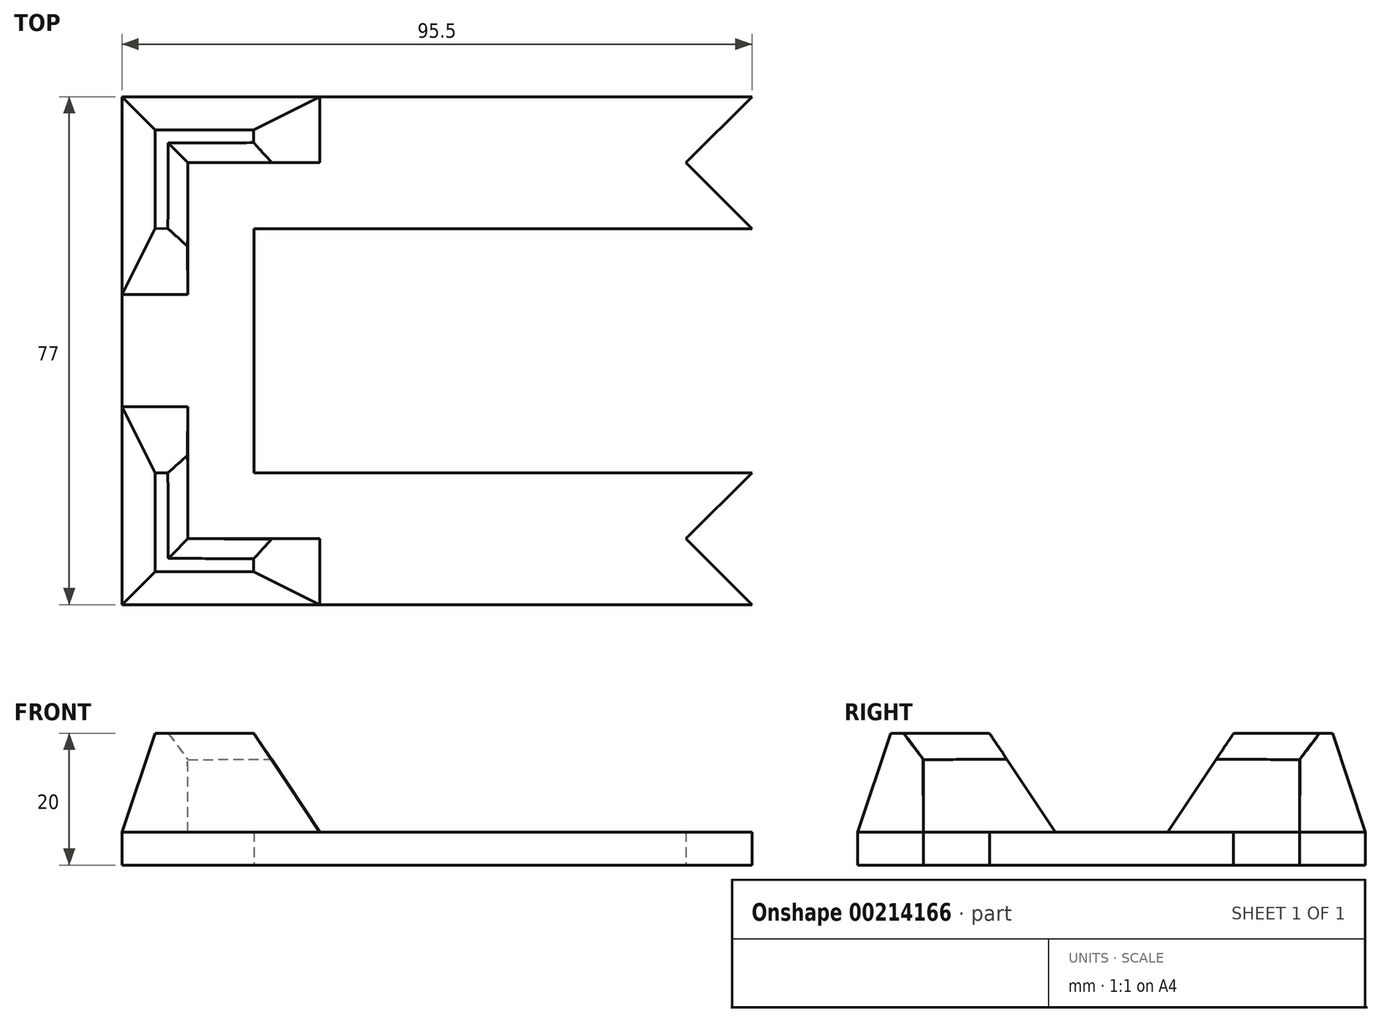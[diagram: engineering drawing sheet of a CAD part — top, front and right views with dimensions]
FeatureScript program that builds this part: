
annotation { "Feature Type Name" : "Feature", "Feature Type Description" : "" }
export const myFeature = defineFeature(function(context is Context, id is Id, definition is map)
    precondition{}
    {
        {
            var Q0;
            Q0=qCreatedBy(makeId("Top.planeOp"),FACE);
            var sketch = newSketch(context, id + "F0", { "sketchPlane" : qUnion([Q0])});
            skLineSegment(sketch, "E0.bottom", {"start": v(75.5, -28.5) * mm, "end": v(-75.5, -28.5) * mm, "construction": true});
            skLineSegment(sketch, "E0.top", {"start": v(75.5, 28.5) * mm, "end": v(-75.5, 28.5) * mm, "construction": true});
            skLineSegment(sketch, "E0.left", {"start": v(75.5, -28.5) * mm, "end": v(75.5, 28.5) * mm, "construction": true});
            skLineSegment(sketch, "E0.right", {"start": v(-75.5, -28.5) * mm, "end": v(-75.5, 28.5) * mm, "construction": true});
            skPoint(sketch, "E0.middle", {"position": v(0, 0) * mm});
            skLineSegment(sketch, "E1.bottom", {"start": v(85.5, -38.5) * mm, "end": v(-85.5, -38.5) * mm});
            skLineSegment(sketch, "E1.top", {"start": v(85.5, 38.5) * mm, "end": v(-85.5, 38.5) * mm});
            skLineSegment(sketch, "E1.left", {"start": v(85.5, -38.5) * mm, "end": v(85.5, 38.5) * mm});
            skLineSegment(sketch, "E1.right", {"start": v(-85.5, -38.5) * mm, "end": v(-85.5, 38.5) * mm});
            skSolve(sketch);
        }
        {
            var Q0;
            Q0=qCreatedBy(makeId("Top.planeOp"),FACE);
            cPlane(context, id + "F1", {"entities" : qUnion([Q0]), "cplaneType" : CPlaneType.OFFSET, "offset" : 15 * mm, "width" : 150 * mm, "height" : 150 * mm});
        }
        {
            var Q0;
            Q0=qCreatedBy(id+"F1.planeOp",FACE);
            var sketch = newSketch(context, id + "F2", { "sketchPlane" : qUnion([Q0])});
            skPoint(sketch, "E2.0", {"position": v(-85.5, -38.5) * mm});
            skPoint(sketch, "E3.0", {"position": v(-75.5, -28.5) * mm});
            skLineSegment(sketch, "E4", {"start": v(-75.58, -18.5) * mm, "end": v(-75.5, -28.5) * mm});
            skLineSegment(sketch, "E5", {"start": v(-75.5, -28.5) * mm, "end": v(-85.5, -38.5) * mm, "construction": true});
            skPoint(sketch, "E6", {"position": v(-80.5, -33.5) * mm});
            skLineSegment(sketch, "E7", {"start": v(-75.58, -18.5) * mm, "end": v(-80.5, -18.54) * mm});
            skLineSegment(sketch, "E8", {"start": v(-80.5, -18.54) * mm, "end": v(-80.5, -33.5) * mm});
            skLineSegment(sketch, "E9.MirrorCS", {"start": v(-65.54, -33.5) * mm, "end": v(-80.5, -33.5) * mm});
            skLineSegment(sketch, "E10.MirrorCS", {"start": v(-65.5, -28.58) * mm, "end": v(-65.54, -33.5) * mm});
            skLineSegment(sketch, "E11.MirrorCS", {"start": v(-65.5, -28.58) * mm, "end": v(-75.5, -28.5) * mm});
            skSolve(sketch);
        }
        {
            var Q0;
            Q0=qCreatedBy(makeId("Top.planeOp"),FACE);
            var sketch = newSketch(context, id + "F3", { "sketchPlane" : qUnion([Q0])});
            skPoint(sketch, "E12.0", {"position": v(-85.5, -38.5) * mm});
            skPoint(sketch, "E13.0", {"position": v(-75.5, -28.5) * mm});
            skLineSegment(sketch, "E14", {"start": v(-85.5, -38.5) * mm, "end": v(-85.5, -8.5) * mm});
            skLineSegment(sketch, "E15", {"start": v(-85.5, -8.5) * mm, "end": v(-75.5, -8.5) * mm});
            skLineSegment(sketch, "E16", {"start": v(-75.5, -8.5) * mm, "end": v(-75.5, -28.5) * mm});
            skLineSegment(sketch, "E17", {"start": v(-75.5, -28.5) * mm, "end": v(-85.5, -38.5) * mm, "construction": true});
            skLineSegment(sketch, "E18.MirrorCS", {"start": v(-55.5, -28.5) * mm, "end": v(-75.5, -28.5) * mm});
            skLineSegment(sketch, "E19.MirrorCS", {"start": v(-85.5, -38.5) * mm, "end": v(-55.5, -38.5) * mm});
            skLineSegment(sketch, "E20.MirrorCS", {"start": v(-55.5, -38.5) * mm, "end": v(-55.5, -28.5) * mm});
            skSolve(sketch);
        }
        {
            var Q0;
            Q0=makeQuery(id+"F0.imprint","IMPRINT",FACE,{"disambiguationData":[TD([[makeQuery(id+"F0.imprint","IMPRINT",EDGE,{"derivedFrom":sQuery(id+"F0.wireOp",EDGE,"E1.bottom")}),-1.0]])]});
            extrude(context, id + "F4", {"entities" : qUnion([Q0]), "oppositeDirection" : true, "depth" : 5 * mm});
        }
        {
            var Q1;
            Q1=makeQuery(id+"F3.imprint","IMPRINT",FACE,{"disambiguationData":[TD([[makeQuery(id+"F3.imprint","IMPRINT",EDGE,{"derivedFrom":sQuery(id+"F3.wireOp",EDGE,"E14")}),-1.0]])]});
            var Q2;
            Q2=makeQuery(id+"F2.imprint","IMPRINT",FACE,{"disambiguationData":[TD([[makeQuery(id+"F2.imprint","IMPRINT",EDGE,{"derivedFrom":sQuery(id+"F2.wireOp",EDGE,"E4")}),-1.0]])]});
            loft(context, id + "F5", {"operationType" : NewBodyOperationType.ADD, "sheetProfilesArray" : [{ "sheetProfileEntities" : qUnion([Q1]) }, { "sheetProfileEntities" : qUnion([Q2]) }]});
        }
        {
            var Q0;
            Q0=makeQuery(id+"F5.opLoft","MID_CAP_EDGE",EDGE,{"disambiguationData":[OSD([sQuery(id+"F2.wireOp",EDGE,"E4"),sQuery(id+"F2.wireOp",EDGE,"E7"),sQuery(id+"F2.wireOp",EDGE,"E11.MirrorCS")])],"capPos":1.0});
            var Q1;
            Q1=makeQuery(id+"F5.opLoft","MID_CAP_EDGE",EDGE,{"disambiguationData":[OSD([sQuery(id+"F2.wireOp",EDGE,"E4"),sQuery(id+"F2.wireOp",EDGE,"E10.MirrorCS"),sQuery(id+"F2.wireOp",EDGE,"E11.MirrorCS")])],"capPos":1.0});
            chamfer(context, id + "F6", {"entities" : qUnion([Q0, Q1]), "chamferType" : ChamferType.TWO_OFFSETS, "width1" : 3 * mm, "oppositeDirection" : false, "width2" : 4 * mm, "tangentPropagation" : true});
        }
        {
            var Q0;
            Q0=makeQuery(id+"F4.opExtrude","SWEPT_BODY",BODY,{"disambiguationData":[OSD([sQuery(id+"F0.wireOp",EDGE,"E1.bottom"),sQuery(id+"F0.wireOp",EDGE,"E1.top"),sQuery(id+"F0.wireOp",EDGE,"E1.left"),sQuery(id+"F0.wireOp",EDGE,"E1.right")])]});
            var Q1;
            Q1=qCreatedBy(makeId("Right.planeOp"),FACE);
            mirror(context, id + "F7", {"operationType" : NewBodyOperationType.ADD, "entities" : qUnion([Q0]), "mirrorPlane" : qUnion([Q1])});
        }
        {
            var Q0;
            Q0=makeQuery(id+"F4.opExtrude","SWEPT_BODY",BODY,{"disambiguationData":[OSD([sQuery(id+"F0.wireOp",EDGE,"E1.bottom"),sQuery(id+"F0.wireOp",EDGE,"E1.top"),sQuery(id+"F0.wireOp",EDGE,"E1.left"),sQuery(id+"F0.wireOp",EDGE,"E1.right")])]});
            var Q1;
            Q1=qCreatedBy(makeId("Front.planeOp"),FACE);
            mirror(context, id + "F8", {"operationType" : NewBodyOperationType.ADD, "entities" : qUnion([Q0]), "mirrorPlane" : qUnion([Q1])});
        }
        {
            var Q0;
            Q0=qCreatedBy(makeId("Top.planeOp"),FACE);
            var sketch = newSketch(context, id + "F9", { "sketchPlane" : qUnion([Q0])});
            skLineSegment(sketch, "E21.bottom", {"start": v(65.5, -18.5) * mm, "end": v(-65.5, -18.5) * mm});
            skLineSegment(sketch, "E21.top", {"start": v(65.5, 18.5) * mm, "end": v(-65.5, 18.5) * mm});
            skLineSegment(sketch, "E21.left", {"start": v(65.5, -18.5) * mm, "end": v(65.5, 18.5) * mm});
            skLineSegment(sketch, "E21.right", {"start": v(-65.5, -18.5) * mm, "end": v(-65.5, 18.5) * mm});
            skPoint(sketch, "E21.middle", {"position": v(0, 0) * mm});
            skLineSegment(sketch, "E22.0", {"start": v(-75.5, -28.5) * mm, "end": v(-75.5, 28.5) * mm, "construction": true});
            skLineSegment(sketch, "E23.0", {"start": v(75.5, 28.5) * mm, "end": v(-75.5, 28.5) * mm, "construction": true});
            skSolve(sketch);
        }
        {
            var Q0;
            Q0=qSketchRegion(id+"F9",true);
            extrude(context, id + "F10", {"entities" : qUnion([Q0]), "operationType" : NewBodyOperationType.REMOVE, "depth" : 25 * mm, "symmetric" : true});
        }
        {
            var Q0;
            Q0=makeQuery(id+"F0.imprint","IMPRINT",FACE,{"disambiguationData":[TD([[makeQuery(id+"F0.imprint","IMPRINT",EDGE,{"derivedFrom":sQuery(id+"F0.wireOp",EDGE,"E1.bottom")}),-1.0]])]});
            var sketch = newSketch(context, id + "F11", { "sketchPlane" : qUnion([Q0])});
            skLineSegment(sketch, "E24.0", {"start": v(75.5, 28.5) * mm, "end": v(-75.5, 28.5) * mm, "construction": true});
            skLineSegment(sketch, "E24.1", {"start": v(-65.5, 18.5) * mm, "end": v(65.5, 18.5) * mm, "construction": true});
            skLineSegment(sketch, "E24.2", {"start": v(85.5, 38.5) * mm, "end": v(-85.5, 38.5) * mm, "construction": true});
            skPoint(sketch, "E24.3", {"position": v(0, 28.5) * mm});
            skLineSegment(sketch, "E25", {"start": v(0, 28.5) * mm, "end": v(18.64, 9.86) * mm});
            skLineSegment(sketch, "E26", {"start": v(18.64, 9.86) * mm, "end": v(18.64, -9.86) * mm});
            skLineSegment(sketch, "E27", {"start": v(18.64, -9.86) * mm, "end": v(0, -28.5) * mm});
            skLineSegment(sketch, "E28", {"start": v(0, -28.5) * mm, "end": v(18.64, -47.14) * mm});
            skLineSegment(sketch, "E29", {"start": v(18.64, -47.14) * mm, "end": v(91.07, -47.14) * mm});
            skLineSegment(sketch, "E30", {"start": v(91.07, -47.14) * mm, "end": v(91.07, 44.05) * mm});
            skLineSegment(sketch, "E31", {"start": v(91.07, 44.05) * mm, "end": v(15.55, 44.05) * mm});
            skLineSegment(sketch, "E32", {"start": v(15.55, 44.05) * mm, "end": v(0, 28.5) * mm});
            skSolve(sketch);
        }
        {
            var Q0;
            {var subQ5=sQuery(id+"F11.wireOp",EDGE,"E25");Q0=makeQuery(id+"F11.imprint","IMPRINT",FACE,{"disambiguationData":[TD([[makeQuery(id+"F11.imprint","IMPRINT",EDGE,{"derivedFrom":subQ5}),1.0]])]});}
            var Q1;
            {var subQ1=sQuery(id+"F11.wireOp",EDGE,"E29");Q1=makeQuery(id+"F11.imprint","IMPRINT",FACE,{"disambiguationData":[TD([[makeQuery(id+"F11.imprint","IMPRINT",EDGE,{"derivedFrom":subQ1}),1.0]])]});}
            extrude(context, id + "F12", {"entities" : qUnion([Q0, Q1]), "depth" : 25 * mm, "hasSecondDirection" : true, "secondDirectionOppositeDirection" : true, "secondDirectionDepth" : 25 * mm});
        }
        {
            var Q0;
            Q0=makeQuery(id+"F12.opExtrude","SWEPT_BODY",BODY,{"disambiguationData":[OSD([sQuery(id+"F11.wireOp",EDGE,"E25"),sQuery(id+"F11.wireOp",EDGE,"E26"),sQuery(id+"F11.wireOp",EDGE,"E27"),sQuery(id+"F11.wireOp",EDGE,"E28"),sQuery(id+"F11.wireOp",EDGE,"E29"),sQuery(id+"F11.wireOp",EDGE,"E30"),sQuery(id+"F11.wireOp",EDGE,"E31"),sQuery(id+"F11.wireOp",EDGE,"E32")])]});
            var Q1;
            Q1=makeQuery(id+"F4.opExtrude","SWEPT_BODY",BODY,{"disambiguationData":[OSD([sQuery(id+"F0.wireOp",EDGE,"E1.bottom"),sQuery(id+"F0.wireOp",EDGE,"E1.top"),sQuery(id+"F0.wireOp",EDGE,"E1.left"),sQuery(id+"F0.wireOp",EDGE,"E1.right")])]});
            booleanBodies(context, id + "F13", {"operationType" : BooleanOperationType.SUBTRACTION, "tools" : qUnion([Q0]), "targets" : qUnion([Q1])});
        }
    });
